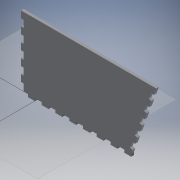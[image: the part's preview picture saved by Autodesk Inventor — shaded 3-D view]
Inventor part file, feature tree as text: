
AUTODESK INVENTOR PART (.ipt)
format: ipt  version: 2019 (Build 230136000, 136)  size: 179,712 bytes
history: native  units: mm
features: reference x9, other x4, extrude x1, sketch x1
ambient origin geometry x8: Origin, YZ Plane, XZ Plane, XY Plane, X Axis, Y Axis, Z Axis, Center Point
bodies: Body1 (feature_tree)
feature tree (15):
  other  "Твердое тело1"
  extrude  "Выдавливание1"  Depth=100.0mm
  sketch  "Эскиз1"
  reference  "Ссылка1"
  reference  "Ссылка2"
  reference  "Ссылка3"
  reference  "Ссылка4"
  reference  "Ссылка5"
  reference  "Ссылка6"
  reference  "Ссылка7"
  reference  "Ссылка8"
  reference  "Ссылка9"
  parser-record x1  (decoder bookkeeping rows leaked as tree rows — omitted from the tree; the rows remain in map.json)
  other  "kowsh.iam"
  other  "Stenka:1"
note: 1 file-system path scrubbed to <path> (originals preserved in map.json)
